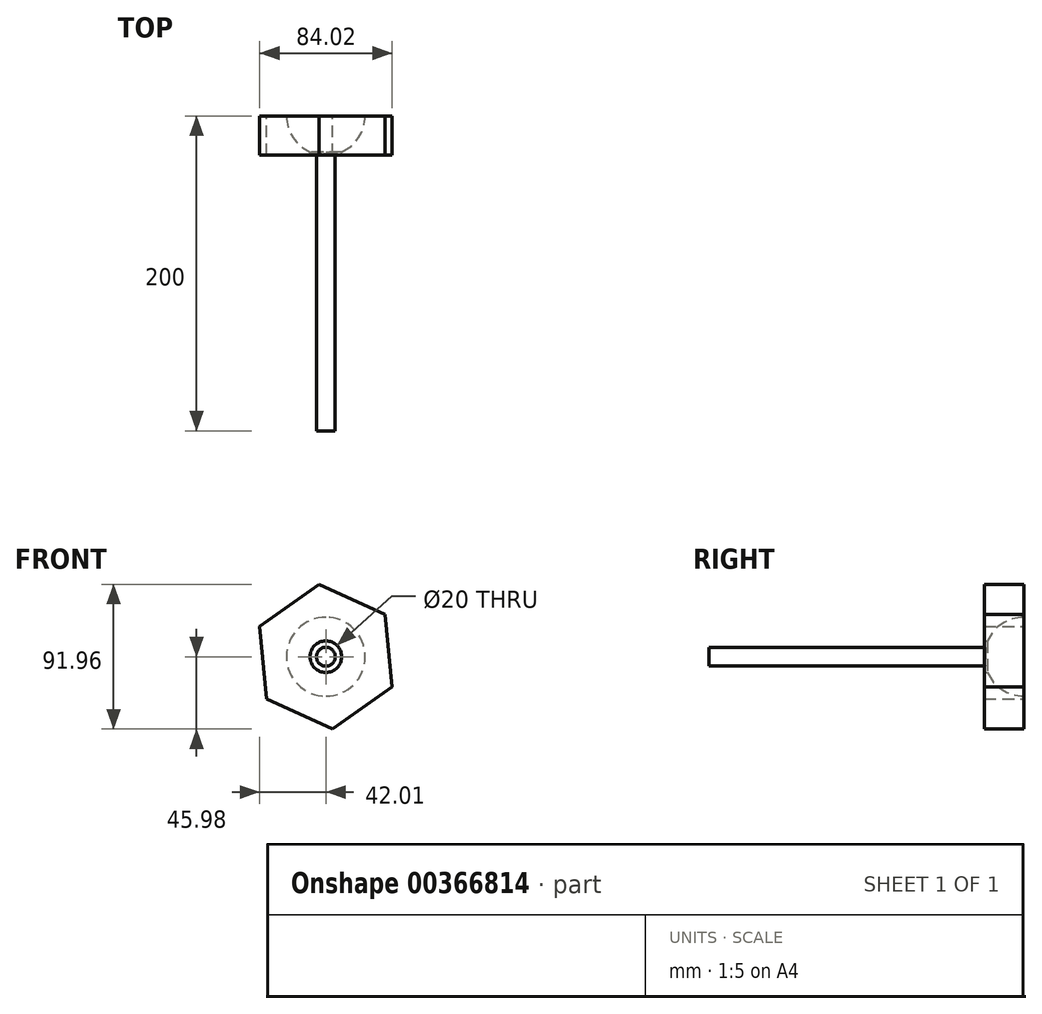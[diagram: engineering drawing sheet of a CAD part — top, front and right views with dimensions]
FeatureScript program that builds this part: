
annotation { "Feature Type Name" : "Feature", "Feature Type Description" : "" }
export const myFeature = defineFeature(function(context is Context, id is Id, definition is map)
    precondition{}
    {
        {
            var Q0;
            Q0=qCreatedBy(makeId("Front.planeOp"),FACE);
            var sketch = newSketch(context, id + "F0", { "sketchPlane" : qUnion([Q0])});
            skArc(sketch, "E0", {"start": v(0, -25) * mm, "mid": v(25, 0) * mm, "end": v(0, 25) * mm});
            skLineSegment(sketch, "E1", {"start": v(0, -25) * mm, "end": v(0, 25) * mm});
            skSolve(sketch);
        }
        {
            var Q0;
            Q0=makeQuery(id+"F0.imprint","IMPRINT",FACE,{"disambiguationData":[TD([[makeQuery(id+"F0.imprint","IMPRINT",EDGE,{"derivedFrom":sQuery(id+"F0.wireOp",EDGE,"E0")}),1.0]])]});
            var Q1;
            Q1=sQuery(id+"F0.wireOp",EDGE,"E1");
            revolve(context, id + "F1", {"entities" : qUnion([Q0]), "axis" : qUnion([Q1]), "revolveType" : RevolveType.FULL});
        }
        {
            var Q0;
            Q0=qCreatedBy(makeId("Front.planeOp"),FACE);
            var sketch = newSketch(context, id + "F2", { "sketchPlane" : qUnion([Q0])});
            skCircle(sketch, "E2", {"center": v(0, 0) * mm, "radius": 6 * mm});
            skSolve(sketch);
        }
        {
            var Q0;
            Q0 = qSketchRegion(id + "F2", true);
            extrude(context, id + "F3", {"entities" : qUnion([Q0]), "operationType" : NewBodyOperationType.ADD, "depth" : 200 * mm});
        }
        {
            var Q0;
            Q0=qCreatedBy(makeId("Front.planeOp"),FACE);
            var sketch = newSketch(context, id + "F4", { "sketchPlane" : qUnion([Q0])});
            skPoint(sketch, "E3.middle", {"position": v(0, 0) * mm});
            skCircle(sketch, "E4", {"center": v(0, 0) * mm, "radius": 10 * mm});
            skCircle(sketch, "E5.cCircle", {"center": v(0, 0) * mm, "radius": 40 * mm, "construction": true});
            skLineSegment(sketch, "E5.0", {"start": v(-37.63, -26.79) * mm, "end": v(-42.01, 19.2) * mm});
            skLineSegment(sketch, "E5.1", {"start": v(-42.01, 19.2) * mm, "end": v(-4.39, 45.98) * mm});
            skLineSegment(sketch, "E5.2", {"start": v(-4.39, 45.98) * mm, "end": v(37.63, 26.79) * mm});
            skLineSegment(sketch, "E5.3", {"start": v(37.63, 26.79) * mm, "end": v(42.01, -19.2) * mm});
            skLineSegment(sketch, "E5.4", {"start": v(42.01, -19.2) * mm, "end": v(4.39, -45.98) * mm});
            skLineSegment(sketch, "E5.5", {"start": v(4.39, -45.98) * mm, "end": v(-37.63, -26.79) * mm});
            skPoint(sketch, "E5.0.midPoint", {"position": v(-39.82, -3.8) * mm});
            skSolve(sketch);
        }
        {
            var Q0;
            Q0 = qSketchRegion(id + "F4", true);
            extrude(context, id + "F5", {"entities" : qUnion([Q0]), "depth" : 25 * mm});
        }
        {
            var Q0;
            Q0=qCreatedBy(makeId("Right.planeOp"),FACE);
            var sketch = newSketch(context, id + "F6", { "sketchPlane" : qUnion([Q0])});
            skArc(sketch, "E6", {"start": v(0, -25) * mm, "mid": v(25, 0) * mm, "end": v(0, 25) * mm});
            skLineSegment(sketch, "E7", {"start": v(0, -25) * mm, "end": v(0, 25) * mm});
            skSolve(sketch);
        }
        {
            var Q0;
            Q0 = qSketchRegion(id + "F6", true);
            var Q1;
            Q1=sQuery(id+"F6.wireOp",EDGE,"E7");
            revolve(context, id + "F7", {"operationType" : NewBodyOperationType.REMOVE, "entities" : qUnion([Q0]), "axis" : qUnion([Q1]), "revolveType" : RevolveType.FULL, "oppositeDirection" : true});
        }
    });
